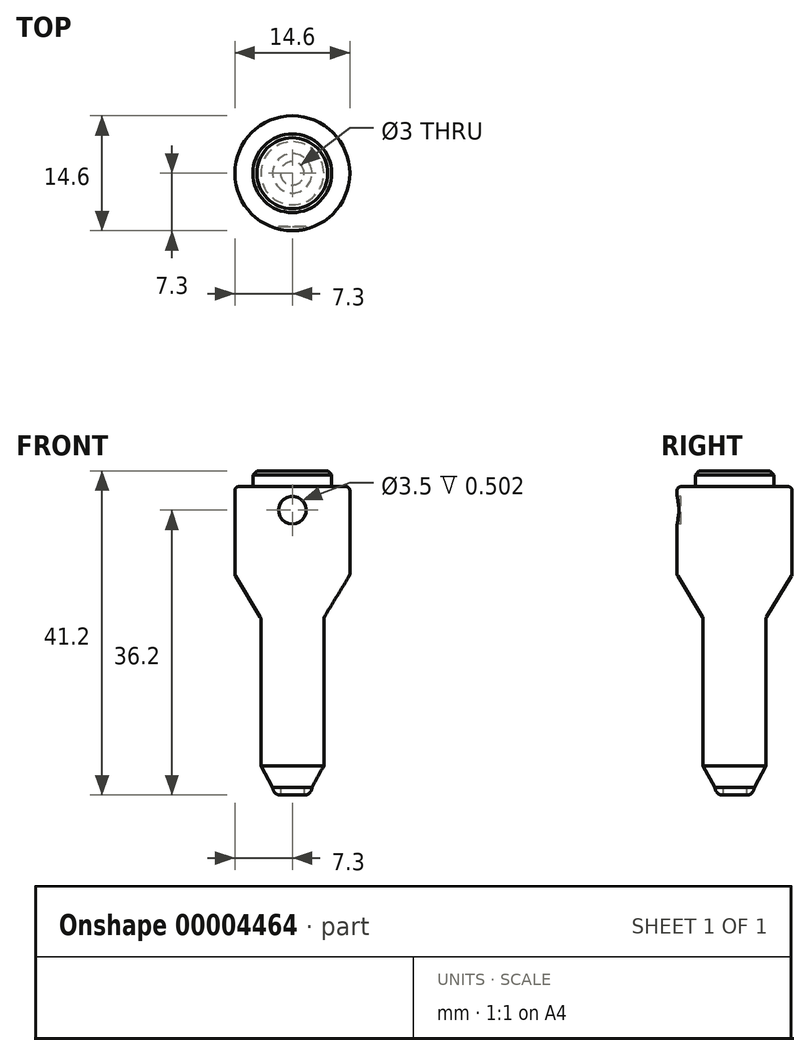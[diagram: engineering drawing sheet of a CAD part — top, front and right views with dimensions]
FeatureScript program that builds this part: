
annotation { "Feature Type Name" : "Feature", "Feature Type Description" : "" }
export const myFeature = defineFeature(function(context is Context, id is Id, definition is map)
    precondition{}
    {
        {
            var Q0;
            Q0=qCreatedBy(makeId("Front.planeOp"),FACE);
            var sketch = newSketch(context, id + "F0", { "sketchPlane" : qUnion([Q0])});
            skLineSegment(sketch, "E0", {"start": v(0, 0) * mm, "end": v(2.5, 0) * mm});
            skLineSegment(sketch, "E1", {"start": v(4, 2.7) * mm, "end": v(4, 21.4) * mm});
            skLineSegment(sketch, "E2", {"start": v(4.07, 21.66) * mm, "end": v(7.23, 26.82) * mm});
            skLineSegment(sketch, "E3", {"start": v(7.3, 27.08) * mm, "end": v(7.3, 37.7) * mm});
            skLineSegment(sketch, "E4", {"start": v(6.8, 38.2) * mm, "end": v(0, 38.2) * mm});
            skLineSegment(sketch, "E5", {"start": v(0, 38.2) * mm, "end": v(0, 0) * mm});
            skPoint(sketch, "E6.visualSharp", {"position": v(7.3, 38.2) * mm});
            skArc(sketch, "E6.filletArc", {"start": v(7.3, 37.7) * mm, "mid": v(7.15, 38.05) * mm, "end": v(6.8, 38.2) * mm});
            skPoint(sketch, "E7.visualSharp", {"position": v(7.3, 26.94) * mm});
            skArc(sketch, "E7.filletArc", {"start": v(7.23, 26.82) * mm, "mid": v(7.28, 26.95) * mm, "end": v(7.3, 27.08) * mm});
            skPoint(sketch, "E8.visualSharp", {"position": v(4, 21.54) * mm});
            skArc(sketch, "E8.filletArc", {"start": v(4.07, 21.66) * mm, "mid": v(4.02, 21.53) * mm, "end": v(4, 21.4) * mm});
            skLineSegment(sketch, "E9", {"start": v(2.5, 0) * mm, "end": v(4, 2.7) * mm});
            skSolve(sketch);
        }
        {
            var Q0;
            Q0=makeQuery(id+"F0.imprint","IMPRINT",FACE,{"disambiguationData":[TD([[makeQuery(id+"F0.imprint","IMPRINT",EDGE,{"derivedFrom":sQuery(id+"F0.wireOp",EDGE,"E0")}),1.0]])]});
            var Q1;
            Q1=sQuery(id+"F0.wireOp",EDGE,"E5");
            revolve(context, id + "F1", {"entities" : qUnion([Q0]), "axis" : qUnion([Q1]), "revolveType" : RevolveType.FULL});
        }
        {
            var Q0;
            Q0=qCreatedBy(makeId("Front.planeOp"),FACE);
            var sketch = newSketch(context, id + "F2", { "sketchPlane" : qUnion([Q0])});
            skLineSegment(sketch, "E10", {"start": v(0, 0) * mm, "end": v(2.5, 0) * mm});
            skLineSegment(sketch, "E11", {"start": v(2.5, 0) * mm, "end": v(2.5, 0) * mm});
            skLineSegment(sketch, "E12", {"start": v(1.5, -1) * mm, "end": v(0, -1) * mm});
            skLineSegment(sketch, "E13", {"start": v(0, -1) * mm, "end": v(0, 0) * mm});
            skPoint(sketch, "E14.visualSharp", {"position": v(2.5, -1) * mm});
            skArc(sketch, "E14.filletArc", {"start": v(1.5, -1) * mm, "mid": v(2.2, -0.7) * mm, "end": v(2.5, 0) * mm});
            skSolve(sketch);
        }
        {
            var Q0;
            Q0=makeQuery(id+"F2.imprint","IMPRINT",FACE,{"disambiguationData":[TD([[makeQuery(id+"F2.imprint","IMPRINT",EDGE,{"derivedFrom":sQuery(id+"F2.wireOp",EDGE,"E10")}),-1.0]])]});
            var Q1;
            Q1=sQuery(id+"F2.wireOp",EDGE,"E13");
            revolve(context, id + "F3", {"entities" : qUnion([Q0]), "axis" : qUnion([Q1]), "revolveType" : RevolveType.FULL});
        }
        {
            var Q0;
            Q0=makeQuery(id+"F3.opRevolve","SWEPT_FACE",FACE,{"disambiguationData":[OSD([sQuery(id+"F2.wireOp",EDGE,"E12")])]});
            var sketch = newSketch(context, id + "F4", { "sketchPlane" : qUnion([Q0])});
            skCircle(sketch, "E15", {"center": v(0, 0) * mm, "radius": 1.5 * mm});
            skSolve(sketch);
        }
        {
            var Q0;
            Q0=makeQuery(id+"F4.imprint","IMPRINT",FACE,{"disambiguationData":[TD([[makeQuery(id+"F4.imprint","IMPRINT",EDGE,{"derivedFrom":sQuery(id+"F4.wireOp",EDGE,"E15")}),1.0]])]});
            extrude(context, id + "F5", {"entities" : qUnion([Q0]), "operationType" : NewBodyOperationType.REMOVE, "endBound" : BoundingType.UP_TO_NEXT, "oppositeDirection" : true, "depth" : 25 * mm});
        }
        {
            var Q0;
            Q0=makeQuery(id+"F1.opRevolve","SWEPT_FACE",FACE,{"disambiguationData":[OSD([sQuery(id+"F0.wireOp",EDGE,"E4")])]});
            var sketch = newSketch(context, id + "F6", { "sketchPlane" : qUnion([Q0])});
            skCircle(sketch, "E16", {"center": v(0, 0) * mm, "radius": 5 * mm});
            skSolve(sketch);
        }
        {
            var Q0;
            Q0=makeQuery(id+"F6.imprint","IMPRINT",FACE,{"disambiguationData":[TD([[makeQuery(id+"F6.imprint","IMPRINT",EDGE,{"derivedFrom":sQuery(id+"F6.wireOp",EDGE,"E16")}),1.0]])]});
            extrude(context, id + "F7", {"entities" : qUnion([Q0]), "depth" : 2 * mm});
        }
        {
            var Q0;
            Q0=makeQuery(id+"F7.opExtrude","CAP_FACE",FACE,{"disambiguationData":[OSD([sQuery(id+"F6.wireOp",EDGE,"E16")])],"isStart":false});
            chamfer(context, id + "F8", {"entities" : qUnion([Q0]), "width" : 0.5 * mm, "tangentPropagation" : true});
        }
        {
            var Q0;
            Q0=qCreatedBy(makeId("Front.planeOp"),FACE);
            cPlane(context, id + "F9", {"entities" : qUnion([Q0]), "cplaneType" : CPlaneType.OFFSET, "offset" : 7.3 * mm, "width" : 150 * mm, "height" : 150 * mm});
        }
        {
            var Q0;
            Q0=qCreatedBy(id+"F9.planeOp",FACE);
            var sketch = newSketch(context, id + "F10", { "sketchPlane" : qUnion([Q0])});
            skCircle(sketch, "E17", {"center": v(0, 35.2) * mm, "radius": 1.75 * mm});
            skSolve(sketch);
        }
        {
            var Q0;
            Q0=makeQuery(id+"F10.imprint","IMPRINT",FACE,{"disambiguationData":[TD([[makeQuery(id+"F10.imprint","IMPRINT",EDGE,{"derivedFrom":sQuery(id+"F10.wireOp",EDGE,"E17")}),1.0]])]});
            extrude(context, id + "F11", {"entities" : qUnion([Q0]), "operationType" : NewBodyOperationType.REMOVE, "oppositeDirection" : true, "depth" : 0.5 * mm});
        }
    });
